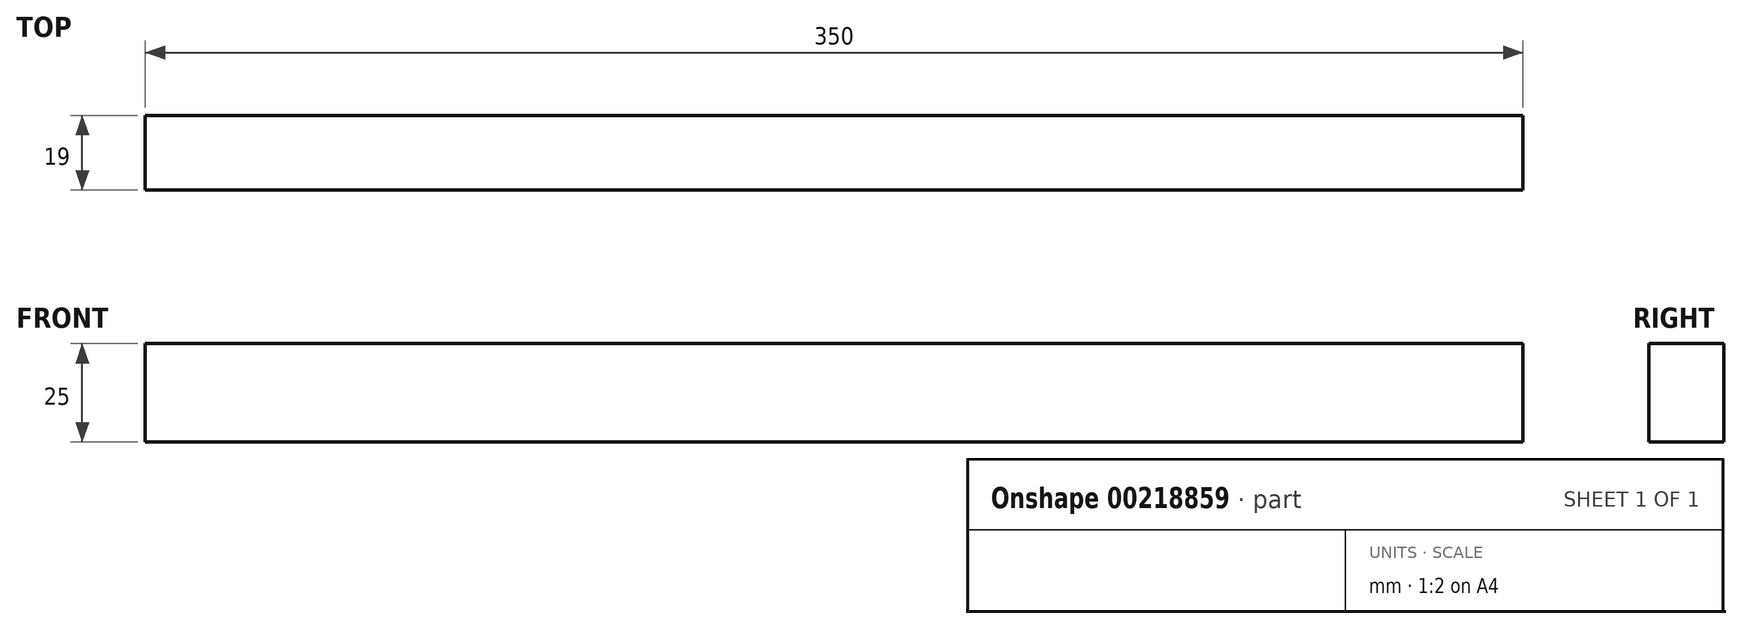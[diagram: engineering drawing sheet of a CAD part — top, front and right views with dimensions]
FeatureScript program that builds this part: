
annotation { "Feature Type Name" : "Feature", "Feature Type Description" : "" }
export const myFeature = defineFeature(function(context is Context, id is Id, definition is map)
    precondition{}
    {
        {
            var Q0;
            Q0=qCreatedBy(makeId("Front.planeOp"),FACE);
            var sketch = newSketch(context, id + "F0", { "sketchPlane" : qUnion([Q0])});
            skLineSegment(sketch, "E0.bottom", {"start": v(175, 12.5) * mm, "end": v(-175, 12.5) * mm});
            skLineSegment(sketch, "E0.top", {"start": v(175, -12.5) * mm, "end": v(-175, -12.5) * mm});
            skLineSegment(sketch, "E0.left", {"start": v(175, 12.5) * mm, "end": v(175, -12.5) * mm});
            skLineSegment(sketch, "E0.right", {"start": v(-175, 12.5) * mm, "end": v(-175, -12.5) * mm});
            skPoint(sketch, "E0.middle", {"position": v(0, 0) * mm});
            skSolve(sketch);
        }
        {
            var Q0;
            Q0=makeQuery(id+"F0.imprint","IMPRINT",FACE,{"disambiguationData":[TD([[makeQuery(id+"F0.imprint","IMPRINT",EDGE,{"derivedFrom":sQuery(id+"F0.wireOp",EDGE,"E0.bottom")}),1.0]])]});
            extrude(context, id + "F1", {"entities" : qUnion([Q0]), "depth" : 19 * mm});
        }
    });
